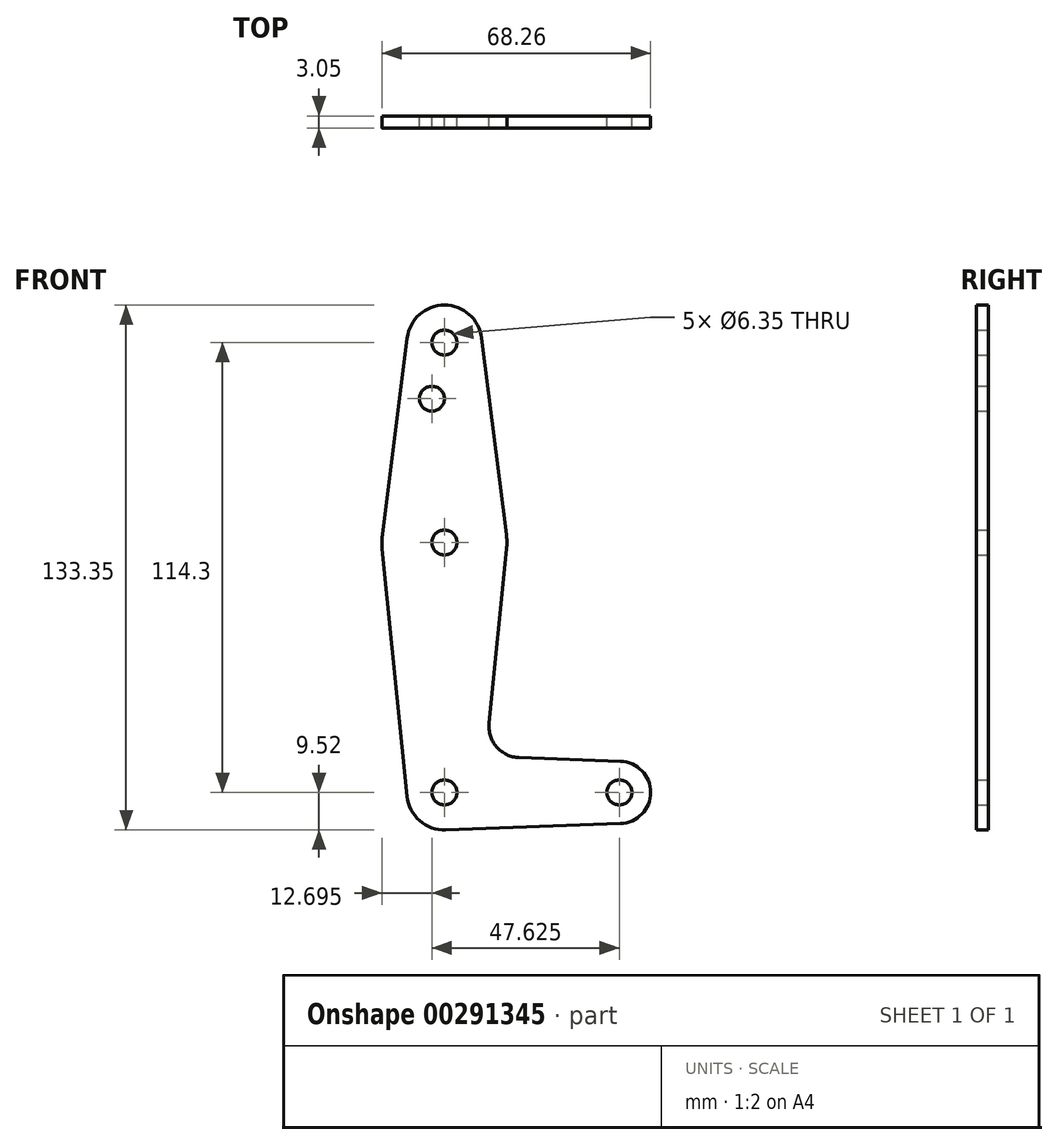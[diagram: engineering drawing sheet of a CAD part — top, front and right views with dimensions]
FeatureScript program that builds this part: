
annotation { "Feature Type Name" : "Feature", "Feature Type Description" : "" }
export const myFeature = defineFeature(function(context is Context, id is Id, definition is map)
    precondition{}
    {
        {
            var Q0;
            Q0=qCreatedBy(makeId("Front.planeOp"),FACE);
            var sketch = newSketch(context, id + "F0", { "sketchPlane" : qUnion([Q0])});
            skCircle(sketch, "E0", {"center": v(0, 0) * mm, "radius": 9.53 * mm});
            skCircle(sketch, "E1", {"center": v(44.45, 0) * mm, "radius": 7.94 * mm});
            skCircle(sketch, "E2", {"center": v(0, 63.5) * mm, "radius": 15.88 * mm});
            skCircle(sketch, "E3", {"center": v(0, 114.3) * mm, "radius": 9.53 * mm});
            skLineSegment(sketch, "E4", {"start": v(0, 114.3) * mm, "end": v(0, 63.5) * mm, "construction": true});
            skLineSegment(sketch, "E5", {"start": v(0, 63.5) * mm, "end": v(0, 0) * mm, "construction": true});
            skLineSegment(sketch, "E6", {"start": v(0, 0) * mm, "end": v(44.45, 0) * mm, "construction": true});
            skLineSegment(sketch, "E7", {"start": v(-15.75, 65.48) * mm, "end": v(-9.45, 115.5) * mm});
            skLineSegment(sketch, "E8", {"start": v(15.75, 65.48) * mm, "end": v(9.45, 115.5) * mm});
            skLineSegment(sketch, "E9", {"start": v(-15.8, 61.91) * mm, "end": v(-9.48, -0.95) * mm});
            skLineSegment(sketch, "E10", {"start": v(15.8, 61.91) * mm, "end": v(11.34, 17.6) * mm});
            skLineSegment(sketch, "E11", {"start": v(44.73, 7.93) * mm, "end": v(18.97, 8.85) * mm});
            skLineSegment(sketch, "E12", {"start": v(44.73, -7.93) * mm, "end": v(0.34, -9.52) * mm});
            skCircle(sketch, "E13", {"center": v(44.45, 0) * mm, "radius": 3.18 * mm});
            skCircle(sketch, "E14", {"center": v(0, 0) * mm, "radius": 3.18 * mm});
            skCircle(sketch, "E15", {"center": v(0, 63.5) * mm, "radius": 3.18 * mm});
            skCircle(sketch, "E16", {"center": v(0, 114.3) * mm, "radius": 3.18 * mm});
            skCircle(sketch, "E17", {"center": v(-3.17, 100.03) * mm, "radius": 3.18 * mm});
            skArc(sketch, "E18.filletArc", {"start": v(11.34, 17.6) * mm, "mid": v(13.26, 11.57) * mm, "end": v(18.97, 8.85) * mm});
            skSolve(sketch);
        }
        {
            var Q0;
            Q0 = qSketchRegion(id + "F0", true);
            extrude(context, id + "F1", {"entities" : qUnion([Q0]), "depth" : 3.05 * mm});
        }
    });
